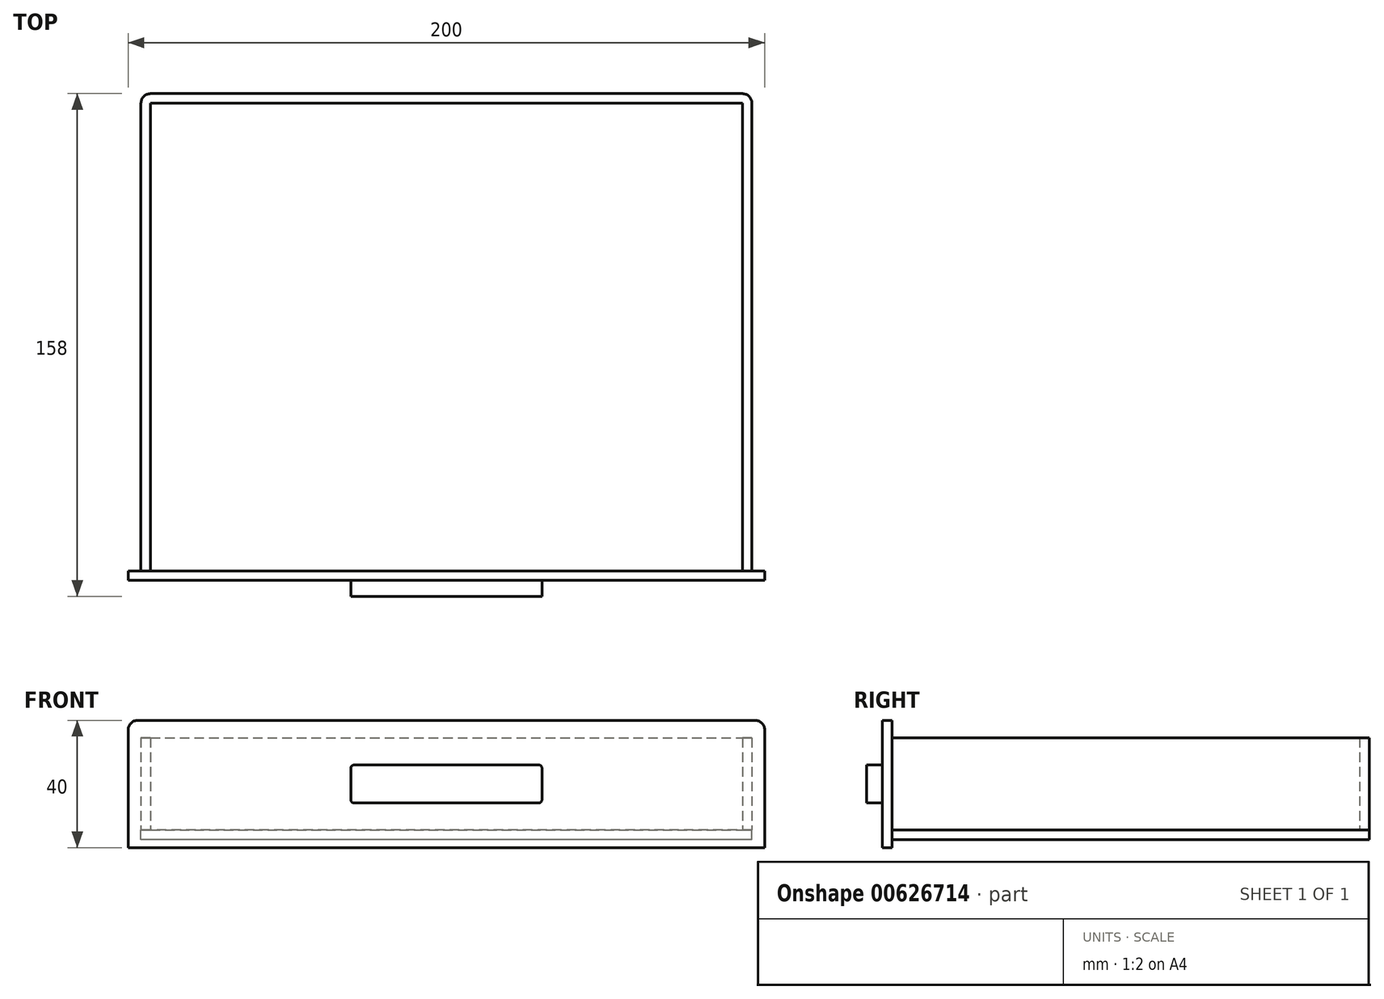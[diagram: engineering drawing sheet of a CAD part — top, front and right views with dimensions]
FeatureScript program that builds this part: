
annotation { "Feature Type Name" : "Feature", "Feature Type Description" : "" }
export const myFeature = defineFeature(function(context is Context, id is Id, definition is map)
    precondition{}
    {
        {
            var Q0;
            Q0=qCreatedBy(makeId("Top.planeOp"),FACE);
            var sketch = newSketch(context, id + "F0", { "sketchPlane" : qUnion([Q0])});
            skLineSegment(sketch, "E0.bottom", {"start": v(-93, 75) * mm, "end": v(93, 75) * mm});
            skLineSegment(sketch, "E0.left", {"start": v(-96, 72) * mm, "end": v(-96, -75) * mm});
            skLineSegment(sketch, "E0.right", {"start": v(96, 72) * mm, "end": v(96, -75) * mm});
            skPoint(sketch, "E0.middle", {"position": v(0, 0) * mm});
            skPoint(sketch, "E1.visualSharp", {"position": v(-96, 75) * mm});
            skArc(sketch, "E1.filletArc", {"start": v(-93, 75) * mm, "mid": v(-95.12, 74.12) * mm, "end": v(-96, 72) * mm});
            skPoint(sketch, "E2.visualSharp", {"position": v(96, 75) * mm});
            skArc(sketch, "E2.filletArc", {"start": v(96, 72) * mm, "mid": v(95.12, 74.12) * mm, "end": v(93, 75) * mm});
            skLineSegment(sketch, "E3.0", {"start": v(-93, 72) * mm, "end": v(-93, -75) * mm});
            skLineSegment(sketch, "E4.0", {"start": v(-93, 72) * mm, "end": v(93, 72) * mm});
            skLineSegment(sketch, "E5.0", {"start": v(93, 72) * mm, "end": v(93, -75) * mm});
            skLineSegment(sketch, "E6", {"start": v(93, -75) * mm, "end": v(96, -75) * mm});
            skLineSegment(sketch, "E7", {"start": v(-96, -75) * mm, "end": v(-93, -75) * mm});
            skSolve(sketch);
        }
        {
            var Q0;
            Q0=makeQuery(id+"F0.imprint","IMPRINT",FACE,{"disambiguationData":[TD([[makeQuery(id+"F0.imprint","IMPRINT",EDGE,{"derivedFrom":sQuery(id+"F0.wireOp",EDGE,"E0.bottom")}),-1.0]])]});
            extrude(context, id + "F1", {"entities" : qUnion([Q0]), "depth" : (29 / 2) * mm, "offsetDistance" : 25 * mm, "hasSecondDirection" : true, "secondDirectionOppositeDirection" : true, "secondDirectionDepth" : (29 / 2) * mm});
        }
        {
            var Q0;
            Q0=qCreatedBy(makeId("Front.planeOp"),FACE);
            cPlane(context, id + "F2", {"entities" : qUnion([Q0]), "cplaneType" : CPlaneType.OFFSET, "offset" : (150 / 2) * mm, "width" : 150 * mm, "height" : 150 * mm});
        }
        {
            var Q0;
            Q0=qCreatedBy(id+"F2.planeOp",FACE);
            var sketch = newSketch(context, id + "F3", { "sketchPlane" : qUnion([Q0])});
            skLineSegment(sketch, "E8.bottom", {"start": v(-97, 20) * mm, "end": v(97, 20) * mm});
            skLineSegment(sketch, "E8.top", {"start": v(-100, -20) * mm, "end": v(100, -20) * mm});
            skLineSegment(sketch, "E8.left", {"start": v(-100, 17) * mm, "end": v(-100, -20) * mm});
            skLineSegment(sketch, "E8.right", {"start": v(100, 17) * mm, "end": v(100, -20) * mm});
            skPoint(sketch, "E8.middle", {"position": v(0, 0) * mm});
            skPoint(sketch, "E9.visualSharp", {"position": v(-100, 20) * mm});
            skArc(sketch, "E9.filletArc", {"start": v(-97, 20) * mm, "mid": v(-99.12, 19.12) * mm, "end": v(-100, 17) * mm});
            skPoint(sketch, "E10.visualSharp", {"position": v(100, 20) * mm});
            skArc(sketch, "E10.filletArc", {"start": v(100, 17) * mm, "mid": v(99.12, 19.12) * mm, "end": v(97, 20) * mm});
            skSolve(sketch);
        }
        {
            var Q0;
            Q0=makeQuery(id+"F3.imprint","IMPRINT",FACE,{"disambiguationData":[TD([[makeQuery(id+"F3.imprint","IMPRINT",EDGE,{"derivedFrom":sQuery(id+"F3.wireOp",EDGE,"E8.bottom")}),-1.0]])]});
            extrude(context, id + "F4", {"entities" : qUnion([Q0]), "depth" : 3 * mm, "offsetDistance" : 25 * mm});
        }
        {
            var Q0;
            Q0=qCreatedBy(makeId("Top.planeOp"),FACE);
            cPlane(context, id + "F5", {"entities" : qUnion([Q0]), "cplaneType" : CPlaneType.OFFSET, "offset" : (29 / 2) * mm, "oppositeDirection" : true, "width" : 150 * mm, "height" : 150 * mm});
        }
        {
            var Q0;
            Q0=qCreatedBy(id+"F5.planeOp",FACE);
            var sketch = newSketch(context, id + "F6", { "sketchPlane" : qUnion([Q0])});
            skLineSegment(sketch, "E11.bottom", {"start": v(93, 75) * mm, "end": v(-93, 75) * mm});
            skLineSegment(sketch, "E11.top", {"start": v(96, -75) * mm, "end": v(-96, -75) * mm});
            skLineSegment(sketch, "E11.left", {"start": v(96, 72) * mm, "end": v(96, -75) * mm});
            skLineSegment(sketch, "E11.right", {"start": v(-96, 72) * mm, "end": v(-96, -75) * mm});
            skPoint(sketch, "E11.middle", {"position": v(0, 0) * mm});
            skPoint(sketch, "E12.visualSharp", {"position": v(96, 75) * mm});
            skArc(sketch, "E12.filletArc", {"start": v(96, 72) * mm, "mid": v(95.12, 74.12) * mm, "end": v(93, 75) * mm});
            skPoint(sketch, "E13.visualSharp", {"position": v(-96, 75) * mm});
            skArc(sketch, "E13.filletArc", {"start": v(-93, 75) * mm, "mid": v(-95.12, 74.12) * mm, "end": v(-96, 72) * mm});
            skSolve(sketch);
        }
        {
            var Q0;
            Q0=makeQuery(id+"F6.imprint","IMPRINT",FACE,{"disambiguationData":[TD([[makeQuery(id+"F6.imprint","IMPRINT",EDGE,{"derivedFrom":sQuery(id+"F6.wireOp",EDGE,"E11.bottom")}),1.0]])]});
            extrude(context, id + "F7", {"entities" : qUnion([Q0]), "oppositeDirection" : true, "depth" : 3 * mm, "offsetDistance" : 25 * mm});
        }
        {
            var Q0;
            Q0=makeQuery(id+"F4.opExtrude","CAP_FACE",FACE,{"disambiguationData":[OSD([sQuery(id+"F3.wireOp",EDGE,"E8.bottom"),sQuery(id+"F3.wireOp",EDGE,"E8.top"),sQuery(id+"F3.wireOp",EDGE,"E8.left"),sQuery(id+"F3.wireOp",EDGE,"E8.right"),sQuery(id+"F3.wireOp",EDGE,"E9.filletArc"),sQuery(id+"F3.wireOp",EDGE,"E10.filletArc")])],"isStart":false});
            var sketch = newSketch(context, id + "F8", { "sketchPlane" : qUnion([Q0])});
            skLineSegment(sketch, "E14.bottom", {"start": v(29, 6) * mm, "end": v(-29, 6) * mm});
            skLineSegment(sketch, "E14.top", {"start": v(29, -6) * mm, "end": v(-29, -6) * mm});
            skLineSegment(sketch, "E14.left", {"start": v(30, 5) * mm, "end": v(30, -5) * mm});
            skLineSegment(sketch, "E14.right", {"start": v(-30, 5) * mm, "end": v(-30, -5) * mm});
            skPoint(sketch, "E14.middle", {"position": v(0, 0) * mm});
            skPoint(sketch, "E15.visualSharp", {"position": v(-30, 6) * mm});
            skArc(sketch, "E15.filletArc", {"start": v(-29, 6) * mm, "mid": v(-29.7, 5.7) * mm, "end": v(-30, 5) * mm});
            skPoint(sketch, "E16.visualSharp", {"position": v(30, 6) * mm});
            skArc(sketch, "E16.filletArc", {"start": v(30, 5) * mm, "mid": v(29.7, 5.7) * mm, "end": v(29, 6) * mm});
            skPoint(sketch, "E17.visualSharp", {"position": v(30, -6) * mm});
            skArc(sketch, "E17.filletArc", {"start": v(29, -6) * mm, "mid": v(29.7, -5.7) * mm, "end": v(30, -5) * mm});
            skPoint(sketch, "E18.visualSharp", {"position": v(-30, -6) * mm});
            skArc(sketch, "E18.filletArc", {"start": v(-30, -5) * mm, "mid": v(-29.7, -5.7) * mm, "end": v(-29, -6) * mm});
            skSolve(sketch);
        }
        {
            var Q0;
            Q0=makeQuery(id+"F8.imprint","IMPRINT",FACE,{"disambiguationData":[TD([[makeQuery(id+"F8.imprint","IMPRINT",EDGE,{"derivedFrom":sQuery(id+"F8.wireOp",EDGE,"E14.bottom")}),1.0]])]});
            extrude(context, id + "F9", {"entities" : qUnion([Q0]), "depth" : 5 * mm, "offsetDistance" : 25 * mm});
        }
    });
